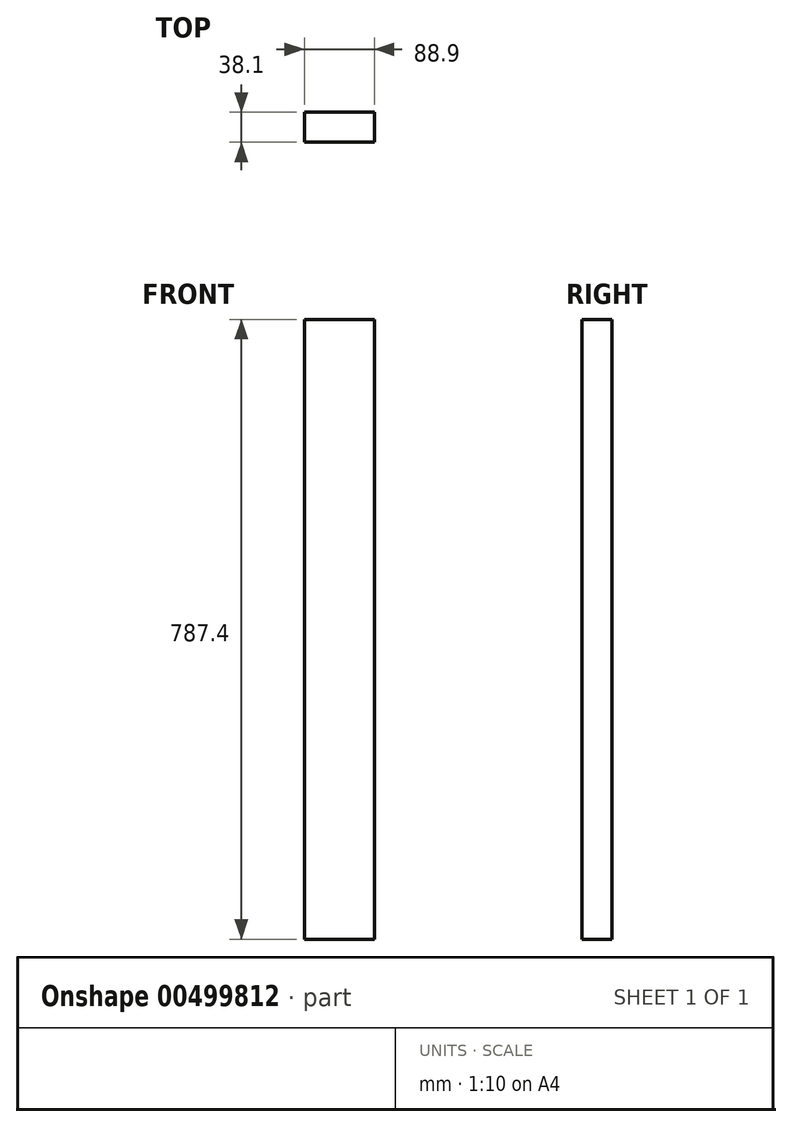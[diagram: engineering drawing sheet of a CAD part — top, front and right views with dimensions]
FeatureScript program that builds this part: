
annotation { "Feature Type Name" : "Feature", "Feature Type Description" : "" }
export const myFeature = defineFeature(function(context is Context, id is Id, definition is map)
    precondition{}
    {
        {
            var Q0;
            Q0=qCreatedBy(makeId("Front.planeOp"),FACE);
            var sketch = newSketch(context, id + "F0", { "sketchPlane" : qUnion([Q0])});
            skLineSegment(sketch, "E0.bottom", {"start": v(44.45, -393.7) * mm, "end": v(-44.45, -393.7) * mm});
            skLineSegment(sketch, "E0.top", {"start": v(44.45, 393.7) * mm, "end": v(-44.45, 393.7) * mm});
            skLineSegment(sketch, "E0.left", {"start": v(44.45, -393.7) * mm, "end": v(44.45, 393.7) * mm});
            skLineSegment(sketch, "E0.right", {"start": v(-44.45, -393.7) * mm, "end": v(-44.45, 393.7) * mm});
            skPoint(sketch, "E0.middle", {"position": v(0, 0) * mm});
            skSolve(sketch);
        }
        {
            var Q0;
            Q0 = qSketchRegion(id + "F0", true);
            extrude(context, id + "F1", {"entities" : qUnion([Q0]), "depth" : 38.1 * mm});
        }
    });
